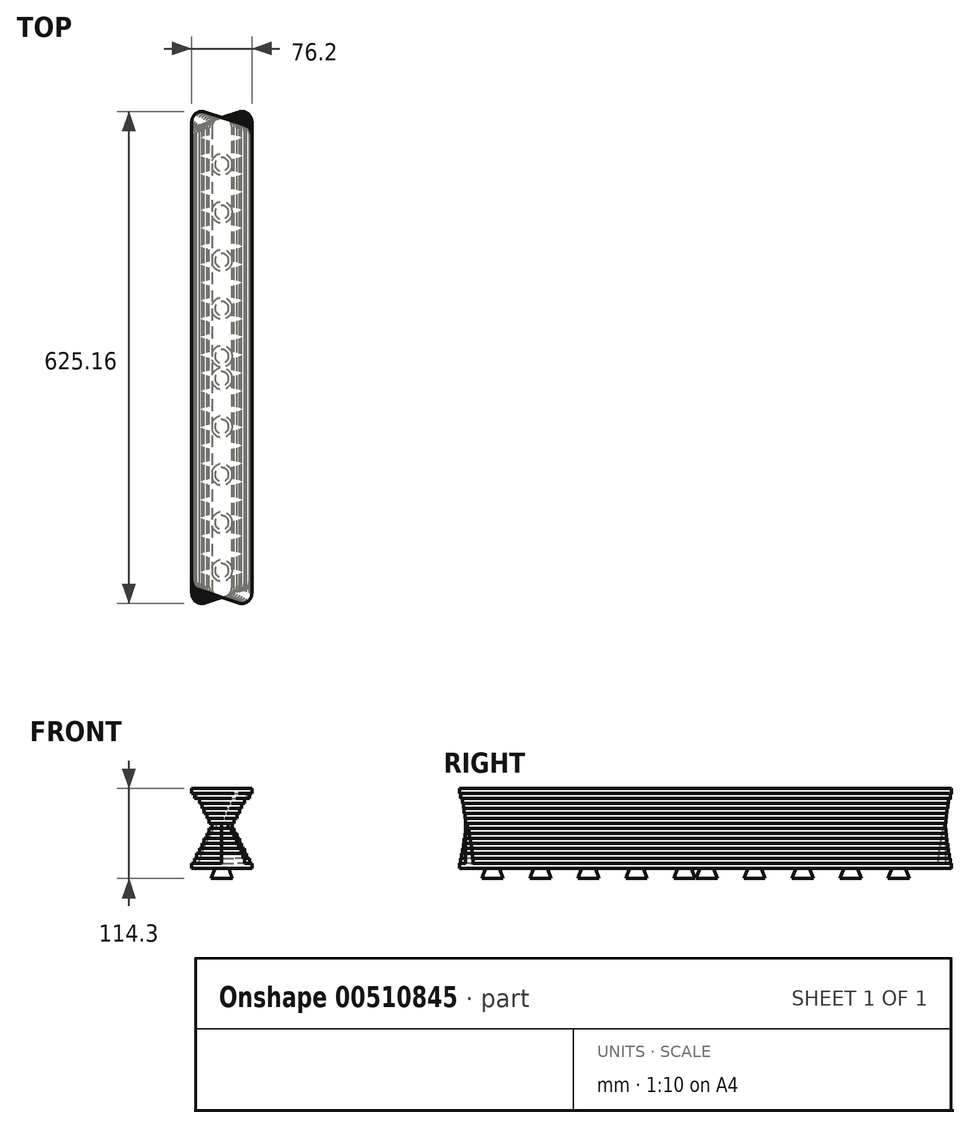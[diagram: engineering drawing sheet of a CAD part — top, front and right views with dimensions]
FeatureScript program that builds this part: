
annotation { "Feature Type Name" : "Feature", "Feature Type Description" : "" }
export const myFeature = defineFeature(function(context is Context, id is Id, definition is map)
    precondition{}
    {
        {
            var Q0;
            Q0=qCreatedBy(makeId("Top.planeOp"),FACE);
            var sketch = newSketch(context, id + "F0", { "sketchPlane" : qUnion([Q0])});
            skPoint(sketch, "E0", {"position": v(0, 0) * mm});
            skPoint(sketch, "E1", {"position": v(-38.1, 0) * mm});
            skPoint(sketch, "E2", {"position": v(-38.1, -304.8) * mm});
            skPoint(sketch, "E3", {"position": v(38.1, 0) * mm});
            skPoint(sketch, "E4", {"position": v(38.1, -279.4) * mm});
            skLineSegment(sketch, "E5", {"start": v(-38.1, 0) * mm, "end": v(-38.1, -287.18) * mm});
            skLineSegment(sketch, "E6", {"start": v(-21.38, -299.23) * mm, "end": v(29.42, -282.3) * mm});
            skLineSegment(sketch, "E7", {"start": v(38.1, -270.25) * mm, "end": v(38.1, 0) * mm});
            skArc(sketch, "E8.filletArc", {"start": v(-38.1, -287.18) * mm, "mid": v(-32.83, -297.48) * mm, "end": v(-21.38, -299.23) * mm});
            skArc(sketch, "E9.filletArc", {"start": v(29.42, -282.3) * mm, "mid": v(35.7, -277.67) * mm, "end": v(38.1, -270.25) * mm});
            skPoint(sketch, "E10", {"position": v(-38.1, 304.8) * mm});
            skPoint(sketch, "E11", {"position": v(38.1, 330.2) * mm});
            skLineSegment(sketch, "E12", {"start": v(-38.1, 0) * mm, "end": v(-38.1, 295.65) * mm});
            skLineSegment(sketch, "E13", {"start": v(-29.42, 307.7) * mm, "end": v(21.38, 324.63) * mm});
            skLineSegment(sketch, "E14", {"start": v(38.1, 312.58) * mm, "end": v(38.1, 0) * mm});
            skArc(sketch, "E15.filletArc", {"start": v(-29.42, 307.7) * mm, "mid": v(-35.7, 303.07) * mm, "end": v(-38.1, 295.65) * mm});
            skArc(sketch, "E16.filletArc", {"start": v(38.1, 312.58) * mm, "mid": v(32.83, 322.88) * mm, "end": v(21.38, 324.63) * mm});
            skSolve(sketch);
        }
        {
            var Q0;
            Q0=makeQuery(id+"F0.imprint","IMPRINT",FACE,{"disambiguationData":[TD([[makeQuery(id+"F0.imprint","IMPRINT",EDGE,{"derivedFrom":sQuery(id+"F0.wireOp",EDGE,"E5")}),1.0]])]});
            extrude(context, id + "F1", {"entities" : qUnion([Q0]), "depth" : 6.35 * mm});
        }
        {
            var Q0;
            Q0=makeQuery(id+"F1.opExtrude","CAP_FACE",FACE,{"disambiguationData":[OSD([sQuery(id+"F0.wireOp",EDGE,"E5"),sQuery(id+"F0.wireOp",EDGE,"E6"),sQuery(id+"F0.wireOp",EDGE,"E7"),sQuery(id+"F0.wireOp",EDGE,"E8.filletArc"),sQuery(id+"F0.wireOp",EDGE,"E9.filletArc"),sQuery(id+"F0.wireOp",EDGE,"E12"),sQuery(id+"F0.wireOp",EDGE,"E13"),sQuery(id+"F0.wireOp",EDGE,"E14"),sQuery(id+"F0.wireOp",EDGE,"E15.filletArc"),sQuery(id+"F0.wireOp",EDGE,"E16.filletArc")])],"isStart":false});
            var sketch = newSketch(context, id + "F2", { "sketchPlane" : qUnion([Q0])});
            skPoint(sketch, "E17", {"position": v(0, 0) * mm});
            skPoint(sketch, "E18", {"position": v(-34.93, 0) * mm});
            skPoint(sketch, "E19", {"position": v(-34.92, -303.21) * mm});
            skPoint(sketch, "E20", {"position": v(34.93, 0) * mm});
            skPoint(sketch, "E21", {"position": v(34.93, -280.99) * mm});
            skLineSegment(sketch, "E22", {"start": v(-34.93, 0) * mm, "end": v(-34.92, -285.84) * mm});
            skLineSegment(sketch, "E23", {"start": v(-18.37, -297.95) * mm, "end": v(26.08, -283.8) * mm});
            skLineSegment(sketch, "E24", {"start": v(34.93, -271.7) * mm, "end": v(34.93, 0) * mm});
            skArc(sketch, "E25.filletArc", {"start": v(-34.92, -285.84) * mm, "mid": v(-29.72, -296.1) * mm, "end": v(-18.37, -297.95) * mm});
            skArc(sketch, "E26.filletArc", {"start": v(26.08, -283.8) * mm, "mid": v(32.48, -279.2) * mm, "end": v(34.92, -271.7) * mm});
            skPoint(sketch, "E27", {"position": v(-34.93, 306.39) * mm});
            skPoint(sketch, "E28", {"position": v(34.92, 328.61) * mm});
            skLineSegment(sketch, "E29", {"start": v(-34.93, 0) * mm, "end": v(-34.93, 297.1) * mm});
            skLineSegment(sketch, "E30", {"start": v(-26.08, 309.2) * mm, "end": v(18.37, 323.35) * mm});
            skLineSegment(sketch, "E31", {"start": v(34.92, 311.24) * mm, "end": v(34.93, 0) * mm});
            skArc(sketch, "E32.filletArc", {"start": v(-26.08, 309.2) * mm, "mid": v(-32.48, 304.6) * mm, "end": v(-34.93, 297.1) * mm});
            skArc(sketch, "E33.filletArc", {"start": v(34.92, 311.24) * mm, "mid": v(29.72, 321.5) * mm, "end": v(18.37, 323.35) * mm});
            skSolve(sketch);
        }
        {
            var Q0;
            {var subQ8=sQuery(id+"F2.wireOp",EDGE,"E22");Q0=makeQuery(id+"F2.imprint","IMPRINT",FACE,{"disambiguationData":[TD([[makeQuery(id+"F2.imprint","IMPRINT",EDGE,{"derivedFrom":subQ8}),1.0]])]});}
            extrude(context, id + "F3", {"entities" : qUnion([Q0]), "depth" : 6.35 * mm});
        }
        {
            var Q0;
            Q0=makeQuery(id+"F3.opExtrude","CAP_FACE",FACE,{"disambiguationData":[OSD([sQuery(id+"F0.wireOp",EDGE,"E6"),sQuery(id+"F0.wireOp",EDGE,"E13"),sQuery(id+"F2.wireOp",EDGE,"E22"),sQuery(id+"F2.wireOp",EDGE,"E23"),sQuery(id+"F2.wireOp",EDGE,"E24"),sQuery(id+"F2.wireOp",EDGE,"E25.filletArc"),sQuery(id+"F2.wireOp",EDGE,"E26.filletArc"),sQuery(id+"F2.wireOp",EDGE,"E29"),sQuery(id+"F2.wireOp",EDGE,"E30"),sQuery(id+"F2.wireOp",EDGE,"E31"),sQuery(id+"F2.wireOp",EDGE,"E32.filletArc"),sQuery(id+"F2.wireOp",EDGE,"E33.filletArc")])],"isStart":false});
            var sketch = newSketch(context, id + "F4", { "sketchPlane" : qUnion([Q0])});
            skPoint(sketch, "E34", {"position": v(0, 0) * mm});
            skPoint(sketch, "E35", {"position": v(-31.75, 0) * mm});
            skPoint(sketch, "E36", {"position": v(-31.75, -301.63) * mm});
            skPoint(sketch, "E37", {"position": v(31.75, 0) * mm});
            skPoint(sketch, "E38", {"position": v(31.75, -282.58) * mm});
            skLineSegment(sketch, "E39", {"start": v(-31.75, 0) * mm, "end": v(-31.75, -284.56) * mm});
            skLineSegment(sketch, "E40", {"start": v(-15.4, -296.72) * mm, "end": v(22.7, -285.3) * mm});
            skLineSegment(sketch, "E41", {"start": v(31.75, -273.13) * mm, "end": v(31.75, 0) * mm});
            skArc(sketch, "E42.filletArc", {"start": v(-31.75, -284.56) * mm, "mid": v(-26.63, -294.74) * mm, "end": v(-15.4, -296.72) * mm});
            skArc(sketch, "E43.filletArc", {"start": v(22.7, -285.3) * mm, "mid": v(29.24, -280.7) * mm, "end": v(31.75, -273.13) * mm});
            skPoint(sketch, "E44.MirrorP", {"position": v(-461.86, 195.96) * mm});
            skPoint(sketch, "E45", {"position": v(-31.75, 307.98) * mm});
            skPoint(sketch, "E46", {"position": v(31.75, 327.03) * mm});
            skLineSegment(sketch, "E47", {"start": v(-31.75, 0) * mm, "end": v(-31.75, 298.53) * mm});
            skLineSegment(sketch, "E48", {"start": v(-22.7, 310.7) * mm, "end": v(15.4, 322.12) * mm});
            skLineSegment(sketch, "E49", {"start": v(31.75, 309.96) * mm, "end": v(31.75, 0) * mm});
            skArc(sketch, "E50.filletArc", {"start": v(-22.7, 310.7) * mm, "mid": v(-29.24, 306.1) * mm, "end": v(-31.75, 298.53) * mm});
            skArc(sketch, "E51.filletArc", {"start": v(31.75, 309.96) * mm, "mid": v(26.63, 320.14) * mm, "end": v(15.4, 322.12) * mm});
            skSolve(sketch);
        }
        {
            var Q0;
            {var subQ8=sQuery(id+"F4.wireOp",EDGE,"E39");Q0=makeQuery(id+"F4.imprint","IMPRINT",FACE,{"disambiguationData":[TD([[makeQuery(id+"F4.imprint","IMPRINT",EDGE,{"derivedFrom":subQ8}),1.0]])]});}
            extrude(context, id + "F5", {"entities" : qUnion([Q0]), "depth" : 6.35 * mm});
        }
        {
            var Q0;
            Q0=makeQuery(id+"F5.opExtrude","CAP_FACE",FACE,{"disambiguationData":[OSD([sQuery(id+"F0.wireOp",EDGE,"E6"),sQuery(id+"F0.wireOp",EDGE,"E13"),sQuery(id+"F4.wireOp",EDGE,"E39"),sQuery(id+"F4.wireOp",EDGE,"E40"),sQuery(id+"F4.wireOp",EDGE,"E41"),sQuery(id+"F4.wireOp",EDGE,"E42.filletArc"),sQuery(id+"F4.wireOp",EDGE,"E43.filletArc"),sQuery(id+"F4.wireOp",EDGE,"E47"),sQuery(id+"F4.wireOp",EDGE,"E48"),sQuery(id+"F4.wireOp",EDGE,"E49"),sQuery(id+"F4.wireOp",EDGE,"E50.filletArc"),sQuery(id+"F4.wireOp",EDGE,"E51.filletArc")])],"isStart":false});
            var sketch = newSketch(context, id + "F6", { "sketchPlane" : qUnion([Q0])});
            skPoint(sketch, "E52", {"position": v(0, 0) * mm});
            skPoint(sketch, "E53", {"position": v(-28.58, 0) * mm});
            skPoint(sketch, "E54", {"position": v(-28.57, -300.04) * mm});
            skPoint(sketch, "E55", {"position": v(28.58, 0) * mm});
            skPoint(sketch, "E56", {"position": v(28.58, -284.16) * mm});
            skLineSegment(sketch, "E57", {"start": v(-28.58, 0) * mm, "end": v(-28.57, -283.33) * mm});
            skLineSegment(sketch, "E58", {"start": v(-12.48, -295.57) * mm, "end": v(19.27, -286.75) * mm});
            skLineSegment(sketch, "E59", {"start": v(28.58, -274.5) * mm, "end": v(28.58, 0) * mm});
            skArc(sketch, "E60.filletArc", {"start": v(-28.57, -283.33) * mm, "mid": v(-23.56, -293.44) * mm, "end": v(-12.48, -295.57) * mm});
            skArc(sketch, "E61.filletArc", {"start": v(19.27, -286.75) * mm, "mid": v(25.99, -282.2) * mm, "end": v(28.57, -274.5) * mm});
            skPoint(sketch, "E62.MirrorP", {"position": v(-895.77, 331.85) * mm});
            skPoint(sketch, "E63", {"position": v(-28.58, 309.56) * mm});
            skPoint(sketch, "E64", {"position": v(28.57, 325.44) * mm});
            skLineSegment(sketch, "E65", {"start": v(-28.58, 0) * mm, "end": v(-28.58, 299.9) * mm});
            skLineSegment(sketch, "E66", {"start": v(-19.27, 312.15) * mm, "end": v(12.48, 320.97) * mm});
            skLineSegment(sketch, "E67", {"start": v(28.57, 308.73) * mm, "end": v(28.58, 0) * mm});
            skArc(sketch, "E68.filletArc", {"start": v(-19.27, 312.15) * mm, "mid": v(-25.99, 307.6) * mm, "end": v(-28.58, 299.9) * mm});
            skArc(sketch, "E69.filletArc", {"start": v(28.57, 308.73) * mm, "mid": v(23.56, 318.84) * mm, "end": v(12.48, 320.97) * mm});
            skSolve(sketch);
        }
        {
            var Q0;
            Q0=makeQuery(id+"F6.imprint","IMPRINT",FACE,{"disambiguationData":[TD([[makeQuery(id+"F6.imprint","IMPRINT",EDGE,{"derivedFrom":sQuery(id+"F6.wireOp",EDGE,"E57")}),1.0]])]});
            extrude(context, id + "F7", {"entities" : qUnion([Q0]), "depth" : 6.35 * mm});
        }
        {
            var Q0;
            Q0=makeQuery(id+"F7.opExtrude","CAP_FACE",FACE,{"disambiguationData":[OSD([sQuery(id+"F0.wireOp",EDGE,"E6"),sQuery(id+"F0.wireOp",EDGE,"E13"),sQuery(id+"F6.wireOp",EDGE,"E57"),sQuery(id+"F6.wireOp",EDGE,"E58"),sQuery(id+"F6.wireOp",EDGE,"E59"),sQuery(id+"F6.wireOp",EDGE,"E60.filletArc"),sQuery(id+"F6.wireOp",EDGE,"E61.filletArc"),sQuery(id+"F6.wireOp",EDGE,"E65"),sQuery(id+"F6.wireOp",EDGE,"E66"),sQuery(id+"F6.wireOp",EDGE,"E67"),sQuery(id+"F6.wireOp",EDGE,"E68.filletArc"),sQuery(id+"F6.wireOp",EDGE,"E69.filletArc")])],"isStart":false});
            var sketch = newSketch(context, id + "F8", { "sketchPlane" : qUnion([Q0])});
            skPoint(sketch, "E70", {"position": v(0, 0) * mm});
            skPoint(sketch, "E71", {"position": v(-25.4, 0) * mm});
            skPoint(sketch, "E72", {"position": v(-25.4, -298.45) * mm});
            skPoint(sketch, "E73", {"position": v(25.4, 0) * mm});
            skPoint(sketch, "E74", {"position": v(25.4, -285.75) * mm});
            skLineSegment(sketch, "E75", {"start": v(-25.4, 0) * mm, "end": v(-25.4, -282.18) * mm});
            skLineSegment(sketch, "E76", {"start": v(-9.62, -294.5) * mm, "end": v(15.78, -288.15) * mm});
            skLineSegment(sketch, "E77", {"start": v(25.4, -275.83) * mm, "end": v(25.4, 0) * mm});
            skArc(sketch, "E78.filletArc", {"start": v(-25.4, -282.18) * mm, "mid": v(-20.52, -292.2) * mm, "end": v(-9.62, -294.5) * mm});
            skArc(sketch, "E79.filletArc", {"start": v(15.78, -288.15) * mm, "mid": v(22.71, -283.65) * mm, "end": v(25.4, -275.83) * mm});
            skPoint(sketch, "E80.MirrorP", {"position": v(-1189.04, 488.26) * mm});
            skPoint(sketch, "E81", {"position": v(-25.4, 311.15) * mm});
            skPoint(sketch, "E82", {"position": v(25.4, 323.85) * mm});
            skLineSegment(sketch, "E83", {"start": v(-25.4, 0) * mm, "end": v(-25.4, 301.23) * mm});
            skLineSegment(sketch, "E84", {"start": v(-15.78, 313.55) * mm, "end": v(9.62, 319.9) * mm});
            skLineSegment(sketch, "E85", {"start": v(25.4, 307.58) * mm, "end": v(25.4, 0) * mm});
            skArc(sketch, "E86.filletArc", {"start": v(-15.78, 313.55) * mm, "mid": v(-22.71, 309.05) * mm, "end": v(-25.4, 301.23) * mm});
            skArc(sketch, "E87.filletArc", {"start": v(25.4, 307.58) * mm, "mid": v(20.52, 317.6) * mm, "end": v(9.62, 319.9) * mm});
            skSolve(sketch);
        }
        {
            var Q0;
            Q0=makeQuery(id+"F8.imprint","IMPRINT",FACE,{"disambiguationData":[TD([[makeQuery(id+"F8.imprint","IMPRINT",EDGE,{"derivedFrom":sQuery(id+"F8.wireOp",EDGE,"E75")}),1.0]])]});
            extrude(context, id + "F9", {"entities" : qUnion([Q0]), "depth" : 6.35 * mm});
        }
        {
            var Q0;
            Q0=makeQuery(id+"F9.opExtrude","CAP_FACE",FACE,{"disambiguationData":[OSD([sQuery(id+"F0.wireOp",EDGE,"E6"),sQuery(id+"F0.wireOp",EDGE,"E13"),sQuery(id+"F8.wireOp",EDGE,"E75"),sQuery(id+"F8.wireOp",EDGE,"E76"),sQuery(id+"F8.wireOp",EDGE,"E77"),sQuery(id+"F8.wireOp",EDGE,"E78.filletArc"),sQuery(id+"F8.wireOp",EDGE,"E79.filletArc"),sQuery(id+"F8.wireOp",EDGE,"E83"),sQuery(id+"F8.wireOp",EDGE,"E84"),sQuery(id+"F8.wireOp",EDGE,"E85"),sQuery(id+"F8.wireOp",EDGE,"E86.filletArc"),sQuery(id+"F8.wireOp",EDGE,"E87.filletArc")])],"isStart":false});
            var sketch = newSketch(context, id + "F10", { "sketchPlane" : qUnion([Q0])});
            skPoint(sketch, "E88", {"position": v(0, 0) * mm});
            skPoint(sketch, "E89", {"position": v(-22.23, 0) * mm});
            skPoint(sketch, "E90", {"position": v(-22.22, -296.86) * mm});
            skPoint(sketch, "E91", {"position": v(22.23, 0) * mm});
            skPoint(sketch, "E92", {"position": v(22.23, -287.34) * mm});
            skLineSegment(sketch, "E93", {"start": v(-22.23, 0) * mm, "end": v(-22.22, -281.15) * mm});
            skLineSegment(sketch, "E94", {"start": v(-6.86, -293.57) * mm, "end": v(12.19, -289.49) * mm});
            skLineSegment(sketch, "E95", {"start": v(22.23, -277.07) * mm, "end": v(22.23, 0) * mm});
            skArc(sketch, "E96.filletArc", {"start": v(-22.22, -281.15) * mm, "mid": v(-17.5, -291.03) * mm, "end": v(-6.86, -293.57) * mm});
            skArc(sketch, "E97.filletArc", {"start": v(12.19, -289.49) * mm, "mid": v(19.4, -285.05) * mm, "end": v(22.22, -277.07) * mm});
            skPoint(sketch, "E98.MirrorP", {"position": v(-1110.6, 407.11) * mm});
            skPoint(sketch, "E99", {"position": v(-22.23, 312.74) * mm});
            skPoint(sketch, "E100", {"position": v(22.22, 322.26) * mm});
            skLineSegment(sketch, "E101", {"start": v(-22.23, 0) * mm, "end": v(-22.23, 302.47) * mm});
            skLineSegment(sketch, "E102", {"start": v(-12.19, 314.89) * mm, "end": v(6.86, 318.97) * mm});
            skLineSegment(sketch, "E103", {"start": v(22.22, 306.55) * mm, "end": v(22.23, 0) * mm});
            skArc(sketch, "E104.filletArc", {"start": v(-12.19, 314.89) * mm, "mid": v(-19.4, 310.45) * mm, "end": v(-22.23, 302.47) * mm});
            skArc(sketch, "E105.filletArc", {"start": v(22.22, 306.55) * mm, "mid": v(17.5, 316.43) * mm, "end": v(6.86, 318.97) * mm});
            skSolve(sketch);
        }
        {
            var Q0;
            Q0=makeQuery(id+"F10.imprint","IMPRINT",FACE,{"disambiguationData":[TD([[makeQuery(id+"F10.imprint","IMPRINT",EDGE,{"derivedFrom":sQuery(id+"F10.wireOp",EDGE,"E93")}),1.0]])]});
            extrude(context, id + "F11", {"entities" : qUnion([Q0]), "depth" : 6.35 * mm});
        }
        {
            var Q0;
            Q0=makeQuery(id+"F11.opExtrude","CAP_FACE",FACE,{"disambiguationData":[OSD([sQuery(id+"F0.wireOp",EDGE,"E6"),sQuery(id+"F0.wireOp",EDGE,"E13"),sQuery(id+"F10.wireOp",EDGE,"E93"),sQuery(id+"F10.wireOp",EDGE,"E94"),sQuery(id+"F10.wireOp",EDGE,"E95"),sQuery(id+"F10.wireOp",EDGE,"E96.filletArc"),sQuery(id+"F10.wireOp",EDGE,"E97.filletArc"),sQuery(id+"F10.wireOp",EDGE,"E101"),sQuery(id+"F10.wireOp",EDGE,"E102"),sQuery(id+"F10.wireOp",EDGE,"E103"),sQuery(id+"F10.wireOp",EDGE,"E104.filletArc"),sQuery(id+"F10.wireOp",EDGE,"E105.filletArc")])],"isStart":false});
            var sketch = newSketch(context, id + "F12", { "sketchPlane" : qUnion([Q0])});
            skPoint(sketch, "E106", {"position": v(0, 0) * mm});
            skPoint(sketch, "E107", {"position": v(-19.05, 0) * mm});
            skPoint(sketch, "E108", {"position": v(-19.05, -295.28) * mm});
            skPoint(sketch, "E109", {"position": v(19.05, 0) * mm});
            skPoint(sketch, "E110", {"position": v(19.05, -288.93) * mm});
            skLineSegment(sketch, "E111", {"start": v(-19.05, 0) * mm, "end": v(-19.05, -280.28) * mm});
            skLineSegment(sketch, "E112", {"start": v(-4.26, -292.81) * mm, "end": v(8.44, -290.7) * mm});
            skLineSegment(sketch, "E113", {"start": v(19.05, -278.17) * mm, "end": v(19.05, 0) * mm});
            skArc(sketch, "E114.filletArc", {"start": v(-19.05, -280.28) * mm, "mid": v(-14.56, -289.97) * mm, "end": v(-4.26, -292.81) * mm});
            skArc(sketch, "E115.filletArc", {"start": v(8.44, -290.7) * mm, "mid": v(16.04, -286.38) * mm, "end": v(19.05, -278.17) * mm});
            skPoint(sketch, "E116.MirrorP", {"position": v(-1134.4, 517.38) * mm});
            skPoint(sketch, "E117", {"position": v(-19.05, 314.33) * mm});
            skPoint(sketch, "E118", {"position": v(19.05, 320.68) * mm});
            skLineSegment(sketch, "E119", {"start": v(-19.05, 0) * mm, "end": v(-19.05, 303.57) * mm});
            skLineSegment(sketch, "E120", {"start": v(-8.44, 316.1) * mm, "end": v(4.26, 318.21) * mm});
            skLineSegment(sketch, "E121", {"start": v(19.05, 305.68) * mm, "end": v(19.05, 0) * mm});
            skArc(sketch, "E122.filletArc", {"start": v(-8.44, 316.1) * mm, "mid": v(-16.04, 311.78) * mm, "end": v(-19.05, 303.57) * mm});
            skArc(sketch, "E123.filletArc", {"start": v(19.05, 305.68) * mm, "mid": v(14.56, 315.37) * mm, "end": v(4.26, 318.21) * mm});
            skSolve(sketch);
        }
        {
            var Q0;
            {var subQ12=sQuery(id+"F12.wireOp",EDGE,"E113");Q0=makeQuery(id+"F12.imprint","IMPRINT",FACE,{"disambiguationData":[TD([[makeQuery(id+"F12.imprint","IMPRINT",EDGE,{"derivedFrom":subQ12}),1.0]])]});}
            extrude(context, id + "F13", {"entities" : qUnion([Q0]), "depth" : 6.35 * mm});
        }
        {
            var Q0;
            Q0=makeQuery(id+"F13.opExtrude","CAP_FACE",FACE,{"disambiguationData":[OSD([sQuery(id+"F0.wireOp",EDGE,"E6"),sQuery(id+"F0.wireOp",EDGE,"E13"),sQuery(id+"F10.wireOp",EDGE,"E93"),sQuery(id+"F10.wireOp",EDGE,"E96.filletArc"),sQuery(id+"F10.wireOp",EDGE,"E101"),sQuery(id+"F10.wireOp",EDGE,"E102"),sQuery(id+"F10.wireOp",EDGE,"E104.filletArc"),sQuery(id+"F12.wireOp",EDGE,"E112"),sQuery(id+"F12.wireOp",EDGE,"E113"),sQuery(id+"F12.wireOp",EDGE,"E115.filletArc"),sQuery(id+"F12.wireOp",EDGE,"E121"),sQuery(id+"F12.wireOp",EDGE,"E123.filletArc")])],"isStart":false});
            var sketch = newSketch(context, id + "F14", { "sketchPlane" : qUnion([Q0])});
            skPoint(sketch, "E124", {"position": v(0, 0) * mm});
            skPoint(sketch, "E125", {"position": v(-15.88, 0) * mm});
            skPoint(sketch, "E126", {"position": v(-15.87, -293.69) * mm});
            skPoint(sketch, "E127", {"position": v(15.88, 0) * mm});
            skPoint(sketch, "E128", {"position": v(15.88, -290.51) * mm});
            skLineSegment(sketch, "E129", {"start": v(-15.88, 0) * mm, "end": v(-15.87, -279.65) * mm});
            skLineSegment(sketch, "E130", {"start": v(-1.91, -292.3) * mm, "end": v(4.44, -291.66) * mm});
            skLineSegment(sketch, "E131", {"start": v(15.88, -279.02) * mm, "end": v(15.88, 0) * mm});
            skArc(sketch, "E132.filletArc", {"start": v(-15.87, -279.65) * mm, "mid": v(-11.7, -289.07) * mm, "end": v(-1.91, -292.3) * mm});
            skArc(sketch, "E133.filletArc", {"start": v(4.44, -291.66) * mm, "mid": v(12.6, -287.54) * mm, "end": v(15.88, -279.02) * mm});
            skPoint(sketch, "E134.MirrorP", {"position": v(-1354.1, 474.43) * mm});
            skPoint(sketch, "E135", {"position": v(-15.88, 315.91) * mm});
            skPoint(sketch, "E136", {"position": v(15.87, 319.09) * mm});
            skLineSegment(sketch, "E137", {"start": v(-15.88, 0) * mm, "end": v(-15.88, 304.42) * mm});
            skLineSegment(sketch, "E138", {"start": v(-4.44, 317.06) * mm, "end": v(1.91, 317.7) * mm});
            skLineSegment(sketch, "E139", {"start": v(15.87, 305.05) * mm, "end": v(15.88, 0) * mm});
            skArc(sketch, "E140.filletArc", {"start": v(-4.44, 317.06) * mm, "mid": v(-12.6, 312.94) * mm, "end": v(-15.88, 304.42) * mm});
            skArc(sketch, "E141.filletArc", {"start": v(15.87, 305.05) * mm, "mid": v(11.7, 314.47) * mm, "end": v(1.91, 317.7) * mm});
            skSolve(sketch);
        }
        {
            var Q0;
            Q0=makeQuery(id+"F14.imprint","IMPRINT",FACE,{"disambiguationData":[TD([[makeQuery(id+"F14.imprint","IMPRINT",EDGE,{"derivedFrom":sQuery(id+"F14.wireOp",EDGE,"E129")}),1.0]])]});
            extrude(context, id + "F15", {"entities" : qUnion([Q0]), "depth" : 6.35 * mm});
        }
        {
            var Q0;
            Q0=makeQuery(id+"F15.opExtrude","CAP_FACE",FACE,{"disambiguationData":[OSD([sQuery(id+"F0.wireOp",EDGE,"E6"),sQuery(id+"F0.wireOp",EDGE,"E13"),sQuery(id+"F14.wireOp",EDGE,"E129"),sQuery(id+"F14.wireOp",EDGE,"E130"),sQuery(id+"F14.wireOp",EDGE,"E131"),sQuery(id+"F14.wireOp",EDGE,"E132.filletArc"),sQuery(id+"F14.wireOp",EDGE,"E133.filletArc"),sQuery(id+"F14.wireOp",EDGE,"E137"),sQuery(id+"F14.wireOp",EDGE,"E138"),sQuery(id+"F14.wireOp",EDGE,"E139"),sQuery(id+"F14.wireOp",EDGE,"E140.filletArc"),sQuery(id+"F14.wireOp",EDGE,"E141.filletArc")])],"isStart":false});
            var sketch = newSketch(context, id + "F16", { "sketchPlane" : qUnion([Q0])});
            skPoint(sketch, "E142", {"position": v(0, 0) * mm});
            skPoint(sketch, "E143", {"position": v(-12.7, 0) * mm});
            skPoint(sketch, "E144", {"position": v(-12.7, -292.1) * mm});
            skPoint(sketch, "E145", {"position": v(12.7, 0) * mm});
            skPoint(sketch, "E146", {"position": v(12.7, -292.1) * mm});
            skLineSegment(sketch, "E147", {"start": v(-12.7, 0) * mm, "end": v(-12.7, -279.4) * mm});
            skLineSegment(sketch, "E148", {"start": v(0, -292.1) * mm, "end": v(0, -292.1) * mm});
            skLineSegment(sketch, "E149", {"start": v(12.7, -279.4) * mm, "end": v(12.7, 0) * mm});
            skArc(sketch, "E150.filletArc", {"start": v(-12.7, -279.4) * mm, "mid": v(-8.98, -288.38) * mm, "end": v(0, -292.1) * mm});
            skArc(sketch, "E151.filletArc", {"start": v(0, -292.1) * mm, "mid": v(8.98, -288.38) * mm, "end": v(12.7, -279.4) * mm});
            skPoint(sketch, "E152.MirrorP", {"position": v(-1174.77, 259.43) * mm});
            skPoint(sketch, "E153", {"position": v(-12.7, 317.5) * mm});
            skPoint(sketch, "E154", {"position": v(12.7, 317.5) * mm});
            skLineSegment(sketch, "E155", {"start": v(-12.7, 0) * mm, "end": v(-12.7, 304.8) * mm});
            skLineSegment(sketch, "E156", {"start": v(0, 317.5) * mm, "end": v(0, 317.5) * mm});
            skLineSegment(sketch, "E157", {"start": v(12.7, 304.8) * mm, "end": v(12.7, 0) * mm});
            skArc(sketch, "E158.filletArc", {"start": v(0, 317.5) * mm, "mid": v(-8.98, 313.78) * mm, "end": v(-12.7, 304.8) * mm});
            skArc(sketch, "E159.filletArc", {"start": v(12.7, 304.8) * mm, "mid": v(8.98, 313.78) * mm, "end": v(0, 317.5) * mm});
            skSolve(sketch);
        }
        {
            var Q0;
            Q0=makeQuery(id+"F16.imprint","IMPRINT",FACE,{"disambiguationData":[TD([[makeQuery(id+"F16.imprint","IMPRINT",EDGE,{"derivedFrom":sQuery(id+"F16.wireOp",EDGE,"E147")}),1.0]])]});
            extrude(context, id + "F17", {"entities" : qUnion([Q0]), "depth" : 6.35 * mm});
        }
        {
            var Q0;
            Q0=makeQuery(id+"F17.opExtrude","CAP_FACE",FACE,{"disambiguationData":[OSD([sQuery(id+"F0.wireOp",EDGE,"E6"),sQuery(id+"F0.wireOp",EDGE,"E13"),sQuery(id+"F16.wireOp",EDGE,"E147"),sQuery(id+"F16.wireOp",EDGE,"E149"),sQuery(id+"F16.wireOp",EDGE,"E150.filletArc"),sQuery(id+"F16.wireOp",EDGE,"E151.filletArc"),sQuery(id+"F16.wireOp",EDGE,"E155"),sQuery(id+"F16.wireOp",EDGE,"E157"),sQuery(id+"F16.wireOp",EDGE,"E158.filletArc"),sQuery(id+"F16.wireOp",EDGE,"E159.filletArc")])],"isStart":false});
            var sketch = newSketch(context, id + "F18", { "sketchPlane" : qUnion([Q0])});
            skPoint(sketch, "E160", {"position": v(0, 0) * mm});
            skPoint(sketch, "E161", {"position": v(-15.88, 0) * mm});
            skPoint(sketch, "E162", {"position": v(-15.87, -290.51) * mm});
            skPoint(sketch, "E163", {"position": v(15.88, 0) * mm});
            skPoint(sketch, "E164", {"position": v(15.88, -293.69) * mm});
            skLineSegment(sketch, "E165", {"start": v(-15.88, 0) * mm, "end": v(-15.87, -279.02) * mm});
            skLineSegment(sketch, "E166", {"start": v(-4.44, -291.66) * mm, "end": v(1.91, -292.3) * mm});
            skLineSegment(sketch, "E167", {"start": v(15.88, -279.65) * mm, "end": v(15.88, 0) * mm});
            skArc(sketch, "E168.filletArc", {"start": v(-15.87, -279.02) * mm, "mid": v(-12.6, -287.54) * mm, "end": v(-4.44, -291.66) * mm});
            skArc(sketch, "E169.filletArc", {"start": v(1.91, -292.3) * mm, "mid": v(11.7, -289.07) * mm, "end": v(15.87, -279.65) * mm});
            skPoint(sketch, "E170.MirrorP", {"position": v(-1386.88, 490.35) * mm});
            skPoint(sketch, "E171", {"position": v(-15.88, 319.09) * mm});
            skPoint(sketch, "E172", {"position": v(15.87, 315.91) * mm});
            skLineSegment(sketch, "E173", {"start": v(-15.88, 0) * mm, "end": v(-15.88, 305.05) * mm});
            skLineSegment(sketch, "E174", {"start": v(-1.91, 317.7) * mm, "end": v(4.44, 317.06) * mm});
            skLineSegment(sketch, "E175", {"start": v(15.87, 304.42) * mm, "end": v(15.88, 0) * mm});
            skArc(sketch, "E176.filletArc", {"start": v(-1.91, 317.7) * mm, "mid": v(-11.7, 314.47) * mm, "end": v(-15.88, 305.05) * mm});
            skArc(sketch, "E177.filletArc", {"start": v(15.87, 304.42) * mm, "mid": v(12.6, 312.94) * mm, "end": v(4.44, 317.06) * mm});
            skSolve(sketch);
        }
        {
            var Q0;
            Q0=qSketchRegion(id+"F18",true);
            extrude(context, id + "F19", {"entities" : qUnion([Q0]), "depth" : 6.35 * mm});
        }
        {
            var Q0;
            Q0=makeQuery(id+"F19.opExtrude","CAP_FACE",FACE,{"disambiguationData":[OSD([sQuery(id+"F0.wireOp",EDGE,"E6"),sQuery(id+"F0.wireOp",EDGE,"E13"),sQuery(id+"F16.wireOp",EDGE,"E147"),sQuery(id+"F16.wireOp",EDGE,"E149"),sQuery(id+"F16.wireOp",EDGE,"E150.filletArc"),sQuery(id+"F16.wireOp",EDGE,"E151.filletArc"),sQuery(id+"F16.wireOp",EDGE,"E155"),sQuery(id+"F16.wireOp",EDGE,"E157"),sQuery(id+"F16.wireOp",EDGE,"E158.filletArc"),sQuery(id+"F16.wireOp",EDGE,"E159.filletArc"),sQuery(id+"F18.wireOp",EDGE,"E166"),sQuery(id+"F18.wireOp",EDGE,"E174")])],"isStart":false});
            var sketch = newSketch(context, id + "F20", { "sketchPlane" : qUnion([Q0])});
            skPoint(sketch, "E178", {"position": v(0, 0) * mm});
            skPoint(sketch, "E179", {"position": v(-19.05, 0) * mm});
            skPoint(sketch, "E180", {"position": v(-19.05, -288.93) * mm});
            skPoint(sketch, "E181", {"position": v(19.05, 0) * mm});
            skPoint(sketch, "E182", {"position": v(19.05, -295.28) * mm});
            skLineSegment(sketch, "E183", {"start": v(-19.05, 0) * mm, "end": v(-19.05, -278.17) * mm});
            skLineSegment(sketch, "E184", {"start": v(-8.44, -290.7) * mm, "end": v(4.26, -292.81) * mm});
            skLineSegment(sketch, "E185", {"start": v(19.05, -280.28) * mm, "end": v(19.05, 0) * mm});
            skArc(sketch, "E186.filletArc", {"start": v(-19.05, -278.17) * mm, "mid": v(-16.04, -286.38) * mm, "end": v(-8.44, -290.7) * mm});
            skArc(sketch, "E187.filletArc", {"start": v(4.26, -292.81) * mm, "mid": v(14.56, -289.97) * mm, "end": v(19.05, -280.28) * mm});
            skPoint(sketch, "E188.MirrorP", {"position": v(-2251.33, 639) * mm});
            skPoint(sketch, "E189", {"position": v(-19.05, 320.68) * mm});
            skPoint(sketch, "E190", {"position": v(19.05, 314.33) * mm});
            skLineSegment(sketch, "E191", {"start": v(-19.05, 0) * mm, "end": v(-19.05, 305.68) * mm});
            skLineSegment(sketch, "E192", {"start": v(-4.26, 318.21) * mm, "end": v(8.44, 316.1) * mm});
            skLineSegment(sketch, "E193", {"start": v(19.05, 303.57) * mm, "end": v(19.05, 0) * mm});
            skArc(sketch, "E194.filletArc", {"start": v(-4.26, 318.21) * mm, "mid": v(-14.56, 315.37) * mm, "end": v(-19.05, 305.68) * mm});
            skArc(sketch, "E195.filletArc", {"start": v(19.05, 303.57) * mm, "mid": v(16.04, 311.78) * mm, "end": v(8.44, 316.1) * mm});
            skSolve(sketch);
        }
        {
            var Q0;
            Q0=qSketchRegion(id+"F20",true);
            extrude(context, id + "F21", {"entities" : qUnion([Q0]), "depth" : 6.35 * mm});
        }
        {
            var Q0;
            Q0=makeQuery(id+"F21.opExtrude","CAP_FACE",FACE,{"disambiguationData":[OSD([sQuery(id+"F0.wireOp",EDGE,"E6"),sQuery(id+"F0.wireOp",EDGE,"E13"),sQuery(id+"F16.wireOp",EDGE,"E147"),sQuery(id+"F16.wireOp",EDGE,"E149"),sQuery(id+"F16.wireOp",EDGE,"E150.filletArc"),sQuery(id+"F16.wireOp",EDGE,"E151.filletArc"),sQuery(id+"F16.wireOp",EDGE,"E155"),sQuery(id+"F16.wireOp",EDGE,"E157"),sQuery(id+"F16.wireOp",EDGE,"E158.filletArc"),sQuery(id+"F16.wireOp",EDGE,"E159.filletArc"),sQuery(id+"F20.wireOp",EDGE,"E184"),sQuery(id+"F20.wireOp",EDGE,"E192")])],"isStart":false});
            var sketch = newSketch(context, id + "F22", { "sketchPlane" : qUnion([Q0])});
            skPoint(sketch, "E196", {"position": v(0, 0) * mm});
            skPoint(sketch, "E197", {"position": v(-22.23, 0) * mm});
            skPoint(sketch, "E198", {"position": v(-22.22, -287.34) * mm});
            skPoint(sketch, "E199", {"position": v(22.23, 0) * mm});
            skPoint(sketch, "E200", {"position": v(22.23, -296.86) * mm});
            skLineSegment(sketch, "E201", {"start": v(-22.23, 0) * mm, "end": v(-22.22, -277.07) * mm});
            skLineSegment(sketch, "E202", {"start": v(-12.19, -289.49) * mm, "end": v(6.86, -293.57) * mm});
            skLineSegment(sketch, "E203", {"start": v(22.23, -281.15) * mm, "end": v(22.23, 0) * mm});
            skArc(sketch, "E204.filletArc", {"start": v(-22.22, -277.07) * mm, "mid": v(-19.4, -285.05) * mm, "end": v(-12.19, -289.49) * mm});
            skArc(sketch, "E205.filletArc", {"start": v(6.86, -293.57) * mm, "mid": v(17.5, -291.03) * mm, "end": v(22.22, -281.15) * mm});
            skPoint(sketch, "E206.MirrorP", {"position": v(-2054.65, 833.78) * mm});
            skPoint(sketch, "E207", {"position": v(-22.23, 322.26) * mm});
            skPoint(sketch, "E208", {"position": v(22.22, 312.74) * mm});
            skLineSegment(sketch, "E209", {"start": v(-22.23, 0) * mm, "end": v(-22.23, 306.55) * mm});
            skLineSegment(sketch, "E210", {"start": v(-6.86, 318.97) * mm, "end": v(12.19, 314.89) * mm});
            skLineSegment(sketch, "E211", {"start": v(22.22, 302.47) * mm, "end": v(22.23, 0) * mm});
            skArc(sketch, "E212.filletArc", {"start": v(-6.86, 318.97) * mm, "mid": v(-17.5, 316.43) * mm, "end": v(-22.23, 306.55) * mm});
            skArc(sketch, "E213.filletArc", {"start": v(22.22, 302.47) * mm, "mid": v(19.4, 310.45) * mm, "end": v(12.19, 314.89) * mm});
            skSolve(sketch);
        }
        {
            var Q0;
            Q0=qSketchRegion(id+"F22",true);
            extrude(context, id + "F23", {"entities" : qUnion([Q0]), "depth" : 6.35 * mm});
        }
        {
            var Q0;
            Q0=makeQuery(id+"F23.opExtrude","CAP_FACE",FACE,{"disambiguationData":[OSD([sQuery(id+"F22.wireOp",EDGE,"E201"),sQuery(id+"F22.wireOp",EDGE,"E202"),sQuery(id+"F22.wireOp",EDGE,"E203"),sQuery(id+"F22.wireOp",EDGE,"E204.filletArc"),sQuery(id+"F22.wireOp",EDGE,"E205.filletArc"),sQuery(id+"F22.wireOp",EDGE,"E209"),sQuery(id+"F22.wireOp",EDGE,"E210"),sQuery(id+"F22.wireOp",EDGE,"E211"),sQuery(id+"F22.wireOp",EDGE,"E212.filletArc"),sQuery(id+"F22.wireOp",EDGE,"E213.filletArc")])],"isStart":false});
            var sketch = newSketch(context, id + "F24", { "sketchPlane" : qUnion([Q0])});
            skPoint(sketch, "E214", {"position": v(0, 0) * mm});
            skPoint(sketch, "E215", {"position": v(-25.4, 0) * mm});
            skPoint(sketch, "E216", {"position": v(-25.4, -285.75) * mm});
            skPoint(sketch, "E217", {"position": v(25.4, 0) * mm});
            skPoint(sketch, "E218", {"position": v(25.4, -298.45) * mm});
            skLineSegment(sketch, "E219", {"start": v(-25.4, 0) * mm, "end": v(-25.4, -275.83) * mm});
            skLineSegment(sketch, "E220", {"start": v(-15.78, -288.15) * mm, "end": v(9.62, -294.5) * mm});
            skLineSegment(sketch, "E221", {"start": v(25.4, -282.18) * mm, "end": v(25.4, 0) * mm});
            skArc(sketch, "E222.filletArc", {"start": v(-25.4, -275.83) * mm, "mid": v(-22.71, -283.65) * mm, "end": v(-15.78, -288.15) * mm});
            skArc(sketch, "E223.filletArc", {"start": v(9.62, -294.5) * mm, "mid": v(20.52, -292.2) * mm, "end": v(25.4, -282.18) * mm});
            skPoint(sketch, "E224.MirrorP", {"position": v(-1763.83, 631.7) * mm});
            skPoint(sketch, "E225", {"position": v(-25.4, 323.85) * mm});
            skPoint(sketch, "E226", {"position": v(25.4, 311.15) * mm});
            skLineSegment(sketch, "E227", {"start": v(-25.4, 0) * mm, "end": v(-25.4, 307.58) * mm});
            skLineSegment(sketch, "E228", {"start": v(-9.62, 319.9) * mm, "end": v(15.78, 313.55) * mm});
            skLineSegment(sketch, "E229", {"start": v(25.4, 301.23) * mm, "end": v(25.4, 0) * mm});
            skArc(sketch, "E230.filletArc", {"start": v(-9.62, 319.9) * mm, "mid": v(-20.52, 317.6) * mm, "end": v(-25.4, 307.58) * mm});
            skArc(sketch, "E231.filletArc", {"start": v(25.4, 301.23) * mm, "mid": v(22.71, 309.05) * mm, "end": v(15.78, 313.55) * mm});
            skSolve(sketch);
        }
        {
            var Q0;
            Q0=qSketchRegion(id+"F24",true);
            extrude(context, id + "F25", {"entities" : qUnion([Q0]), "depth" : 6.35 * mm});
        }
        {
            var Q0;
            Q0=makeQuery(id+"F25.opExtrude","CAP_FACE",FACE,{"disambiguationData":[OSD([sQuery(id+"F24.wireOp",EDGE,"E219"),sQuery(id+"F24.wireOp",EDGE,"E220"),sQuery(id+"F24.wireOp",EDGE,"E221"),sQuery(id+"F24.wireOp",EDGE,"E222.filletArc"),sQuery(id+"F24.wireOp",EDGE,"E223.filletArc"),sQuery(id+"F24.wireOp",EDGE,"E227"),sQuery(id+"F24.wireOp",EDGE,"E228"),sQuery(id+"F24.wireOp",EDGE,"E229"),sQuery(id+"F24.wireOp",EDGE,"E230.filletArc"),sQuery(id+"F24.wireOp",EDGE,"E231.filletArc")])],"isStart":false});
            var sketch = newSketch(context, id + "F26", { "sketchPlane" : qUnion([Q0])});
            skPoint(sketch, "E232", {"position": v(0, 0) * mm});
            skPoint(sketch, "E233", {"position": v(-28.58, 0) * mm});
            skPoint(sketch, "E234", {"position": v(-28.57, -284.16) * mm});
            skPoint(sketch, "E235", {"position": v(28.58, 0) * mm});
            skPoint(sketch, "E236", {"position": v(28.58, -300.04) * mm});
            skLineSegment(sketch, "E237", {"start": v(-28.58, 0) * mm, "end": v(-28.57, -274.5) * mm});
            skLineSegment(sketch, "E238", {"start": v(-19.27, -286.75) * mm, "end": v(12.48, -295.57) * mm});
            skLineSegment(sketch, "E239", {"start": v(28.58, -283.33) * mm, "end": v(28.58, 0) * mm});
            skArc(sketch, "E240.filletArc", {"start": v(-28.57, -274.5) * mm, "mid": v(-25.99, -282.2) * mm, "end": v(-19.27, -286.75) * mm});
            skArc(sketch, "E241.filletArc", {"start": v(12.48, -295.57) * mm, "mid": v(23.56, -293.44) * mm, "end": v(28.57, -283.33) * mm});
            skPoint(sketch, "E242.MirrorP", {"position": v(-2122.86, 677.9) * mm});
            skPoint(sketch, "E243", {"position": v(-28.58, 325.44) * mm});
            skPoint(sketch, "E244", {"position": v(28.57, 309.56) * mm});
            skLineSegment(sketch, "E245", {"start": v(-28.58, 0) * mm, "end": v(-28.58, 308.73) * mm});
            skLineSegment(sketch, "E246", {"start": v(-12.48, 320.97) * mm, "end": v(19.27, 312.15) * mm});
            skLineSegment(sketch, "E247", {"start": v(28.57, 299.9) * mm, "end": v(28.58, 0) * mm});
            skArc(sketch, "E248.filletArc", {"start": v(-12.48, 320.97) * mm, "mid": v(-23.56, 318.84) * mm, "end": v(-28.58, 308.73) * mm});
            skArc(sketch, "E249.filletArc", {"start": v(28.57, 299.9) * mm, "mid": v(25.99, 307.6) * mm, "end": v(19.27, 312.15) * mm});
            skSolve(sketch);
        }
        {
            var Q0;
            Q0=qSketchRegion(id+"F26",true);
            extrude(context, id + "F27", {"entities" : qUnion([Q0]), "depth" : 6.35 * mm});
        }
        {
            var Q0;
            Q0=makeQuery(id+"F27.opExtrude","CAP_FACE",FACE,{"disambiguationData":[OSD([sQuery(id+"F26.wireOp",EDGE,"E237"),sQuery(id+"F26.wireOp",EDGE,"E238"),sQuery(id+"F26.wireOp",EDGE,"E239"),sQuery(id+"F26.wireOp",EDGE,"E240.filletArc"),sQuery(id+"F26.wireOp",EDGE,"E241.filletArc"),sQuery(id+"F26.wireOp",EDGE,"E245"),sQuery(id+"F26.wireOp",EDGE,"E246"),sQuery(id+"F26.wireOp",EDGE,"E247"),sQuery(id+"F26.wireOp",EDGE,"E248.filletArc"),sQuery(id+"F26.wireOp",EDGE,"E249.filletArc")])],"isStart":false});
            var sketch = newSketch(context, id + "F28", { "sketchPlane" : qUnion([Q0])});
            skPoint(sketch, "E250", {"position": v(0, 0) * mm});
            skPoint(sketch, "E251", {"position": v(-31.75, 0) * mm});
            skPoint(sketch, "E252", {"position": v(-31.75, -282.58) * mm});
            skPoint(sketch, "E253", {"position": v(31.75, 0) * mm});
            skPoint(sketch, "E254", {"position": v(31.75, -301.63) * mm});
            skLineSegment(sketch, "E255", {"start": v(-31.75, 0) * mm, "end": v(-31.75, -273.13) * mm});
            skLineSegment(sketch, "E256", {"start": v(-22.7, -285.3) * mm, "end": v(15.4, -296.72) * mm});
            skLineSegment(sketch, "E257", {"start": v(31.75, -284.56) * mm, "end": v(31.75, 0) * mm});
            skArc(sketch, "E258.filletArc", {"start": v(-31.75, -273.13) * mm, "mid": v(-29.24, -280.7) * mm, "end": v(-22.7, -285.3) * mm});
            skArc(sketch, "E259.filletArc", {"start": v(15.4, -296.72) * mm, "mid": v(26.63, -294.74) * mm, "end": v(31.75, -284.56) * mm});
            skPoint(sketch, "E260.MirrorP", {"position": v(-2131.05, 728.59) * mm});
            skPoint(sketch, "E261", {"position": v(-31.75, 327.03) * mm});
            skPoint(sketch, "E262", {"position": v(31.75, 307.98) * mm});
            skLineSegment(sketch, "E263", {"start": v(-31.75, 0) * mm, "end": v(-31.75, 309.96) * mm});
            skLineSegment(sketch, "E264", {"start": v(-15.4, 322.12) * mm, "end": v(22.7, 310.7) * mm});
            skLineSegment(sketch, "E265", {"start": v(31.75, 298.53) * mm, "end": v(31.75, 0) * mm});
            skArc(sketch, "E266.filletArc", {"start": v(-15.4, 322.12) * mm, "mid": v(-26.63, 320.14) * mm, "end": v(-31.75, 309.96) * mm});
            skArc(sketch, "E267.filletArc", {"start": v(31.75, 298.53) * mm, "mid": v(29.24, 306.1) * mm, "end": v(22.7, 310.7) * mm});
            skSolve(sketch);
        }
        {
            var Q0;
            Q0=qSketchRegion(id+"F28",true);
            extrude(context, id + "F29", {"entities" : qUnion([Q0]), "depth" : 6.35 * mm});
        }
        {
            var Q0;
            {var subQ12=makeQuery(id+"F27.opExtrude","CAP_EDGE",EDGE,{"disambiguationData":[OSD([sQuery(id+"F26.wireOp",EDGE,"E241.filletArc")])],"isStart":false});Q0=makeQuery(id+"F28.imprint","IMPRINT",FACE,{"disambiguationData":[TD([[makeQuery(id+"F28.imprint","IMPRINT",EDGE,{"derivedFrom":subQ12}),1.0]])]});}
            var sketch = newSketch(context, id + "F30", { "sketchPlane" : qUnion([Q0])});
            skPoint(sketch, "E268", {"position": v(0, 0) * mm});
            skPoint(sketch, "E269", {"position": v(-34.93, 0) * mm});
            skPoint(sketch, "E270", {"position": v(-34.93, -280.99) * mm});
            skPoint(sketch, "E271", {"position": v(34.93, 0) * mm});
            skPoint(sketch, "E272", {"position": v(34.93, -303.21) * mm});
            skLineSegment(sketch, "E273", {"start": v(-34.93, 0) * mm, "end": v(-34.93, -271.7) * mm});
            skLineSegment(sketch, "E274", {"start": v(-26.08, -283.8) * mm, "end": v(18.37, -297.95) * mm});
            skLineSegment(sketch, "E275", {"start": v(34.93, -285.84) * mm, "end": v(34.93, 0) * mm});
            skArc(sketch, "E276.filletArc", {"start": v(-34.93, -271.7) * mm, "mid": v(-32.48, -279.2) * mm, "end": v(-26.08, -283.8) * mm});
            skArc(sketch, "E277.filletArc", {"start": v(18.37, -297.95) * mm, "mid": v(29.72, -296.1) * mm, "end": v(34.92, -285.84) * mm});
            skPoint(sketch, "E278.MirrorP", {"position": v(-2087.8, 736.08) * mm});
            skPoint(sketch, "E279", {"position": v(-34.93, 328.61) * mm});
            skPoint(sketch, "E280", {"position": v(34.92, 306.39) * mm});
            skLineSegment(sketch, "E281", {"start": v(-34.93, 0) * mm, "end": v(-34.93, 311.24) * mm});
            skLineSegment(sketch, "E282", {"start": v(-18.37, 323.35) * mm, "end": v(26.08, 309.2) * mm});
            skLineSegment(sketch, "E283", {"start": v(34.92, 297.1) * mm, "end": v(34.93, 0) * mm});
            skArc(sketch, "E284.filletArc", {"start": v(-18.37, 323.35) * mm, "mid": v(-29.72, 321.5) * mm, "end": v(-34.93, 311.24) * mm});
            skArc(sketch, "E285.filletArc", {"start": v(34.92, 297.1) * mm, "mid": v(32.48, 304.6) * mm, "end": v(26.08, 309.2) * mm});
            skSolve(sketch);
        }
        {
            var Q0;
            Q0=qSketchRegion(id+"F30",true);
            extrude(context, id + "F31", {"entities" : qUnion([Q0]), "depth" : 6.35 * mm});
        }
        {
            var Q0;
            Q0=makeQuery(id+"F31.opExtrude","CAP_FACE",FACE,{"disambiguationData":[OSD([sQuery(id+"F30.wireOp",EDGE,"E273"),sQuery(id+"F30.wireOp",EDGE,"E274"),sQuery(id+"F30.wireOp",EDGE,"E275"),sQuery(id+"F30.wireOp",EDGE,"E276.filletArc"),sQuery(id+"F30.wireOp",EDGE,"E277.filletArc"),sQuery(id+"F30.wireOp",EDGE,"E281"),sQuery(id+"F30.wireOp",EDGE,"E282"),sQuery(id+"F30.wireOp",EDGE,"E283"),sQuery(id+"F30.wireOp",EDGE,"E284.filletArc"),sQuery(id+"F30.wireOp",EDGE,"E285.filletArc")])],"isStart":false});
            var sketch = newSketch(context, id + "F32", { "sketchPlane" : qUnion([Q0])});
            skPoint(sketch, "E286", {"position": v(0, 0) * mm});
            skPoint(sketch, "E287", {"position": v(-38.1, 0) * mm});
            skPoint(sketch, "E288", {"position": v(-38.1, -279.4) * mm});
            skPoint(sketch, "E289", {"position": v(38.1, 0) * mm});
            skPoint(sketch, "E290", {"position": v(38.1, -304.8) * mm});
            skLineSegment(sketch, "E291", {"start": v(-38.1, 0) * mm, "end": v(-38.1, -270.25) * mm});
            skLineSegment(sketch, "E292", {"start": v(-29.42, -282.3) * mm, "end": v(21.38, -299.23) * mm});
            skLineSegment(sketch, "E293", {"start": v(38.1, -287.18) * mm, "end": v(38.1, 0) * mm});
            skArc(sketch, "E294.filletArc", {"start": v(-38.1, -270.25) * mm, "mid": v(-35.7, -277.67) * mm, "end": v(-29.42, -282.3) * mm});
            skArc(sketch, "E295.filletArc", {"start": v(21.38, -299.23) * mm, "mid": v(32.83, -297.48) * mm, "end": v(38.1, -287.18) * mm});
            skPoint(sketch, "E296.MirrorP", {"position": v(-2058.68, 783.5) * mm});
            skPoint(sketch, "E297", {"position": v(-38.1, 330.2) * mm});
            skPoint(sketch, "E298", {"position": v(38.1, 304.8) * mm});
            skLineSegment(sketch, "E299", {"start": v(-38.1, 0) * mm, "end": v(-38.1, 312.58) * mm});
            skLineSegment(sketch, "E300", {"start": v(-21.38, 324.63) * mm, "end": v(29.42, 307.7) * mm});
            skLineSegment(sketch, "E301", {"start": v(38.1, 295.65) * mm, "end": v(38.1, 0) * mm});
            skArc(sketch, "E302.filletArc", {"start": v(-21.38, 324.63) * mm, "mid": v(-32.83, 322.88) * mm, "end": v(-38.1, 312.58) * mm});
            skArc(sketch, "E303.filletArc", {"start": v(38.1, 295.65) * mm, "mid": v(35.7, 303.07) * mm, "end": v(29.42, 307.7) * mm});
            skSolve(sketch);
        }
        {
            var Q0;
            Q0=qSketchRegion(id+"F32",true);
            extrude(context, id + "F33", {"entities" : qUnion([Q0]), "depth" : 6.35 * mm});
        }
        {
            var Q0;
            Q0=qCreatedBy(makeId("Top.planeOp"),FACE);
            var sketch = newSketch(context, id + "F34", { "sketchPlane" : qUnion([Q0])});
            skLineSegment(sketch, "E304", {"start": v(0, 0) * mm, "end": v(0, -271) * mm, "construction": true});
            skCircle(sketch, "E305", {"center": v(0, -257.95) * mm, "radius": 8.8 * mm});
            skCircle(sketch, "E306.0.1.0", {"center": v(0, -196.99) * mm, "radius": 8.8 * mm});
            skCircle(sketch, "E306.0.2.0", {"center": v(0, -136.03) * mm, "radius": 8.8 * mm});
            skCircle(sketch, "E306.0.3.0", {"center": v(0, -75.07) * mm, "radius": 8.8 * mm});
            skCircle(sketch, "E306.0.4.0", {"center": v(0, -14.1) * mm, "radius": 8.8 * mm});
            skLineSegment(sketch, "E306.direction1", {"start": v(0, -257.95) * mm, "end": v(25.4, -257.95) * mm, "construction": true});
            skLineSegment(sketch, "E306.direction2", {"start": v(0, -257.95) * mm, "end": v(0, -196.99) * mm, "construction": true});
            skLineSegment(sketch, "E307.MirrorCS", {"start": v(0, 257.95) * mm, "end": v(0, 196.99) * mm, "construction": true});
            skLineSegment(sketch, "E308.MirrorCS", {"start": v(0, 0) * mm, "end": v(0, 271) * mm, "construction": true});
            skLineSegment(sketch, "E309.MirrorCS", {"start": v(0, 257.95) * mm, "end": v(25.4, 257.95) * mm, "construction": true});
            skCircle(sketch, "E310.MirrorC", {"center": v(0, 14.1) * mm, "radius": 8.8 * mm});
            skCircle(sketch, "E311.MirrorC", {"center": v(0, 136.03) * mm, "radius": 8.8 * mm});
            skCircle(sketch, "E312.MirrorC", {"center": v(0, 75.07) * mm, "radius": 8.8 * mm});
            skCircle(sketch, "E313.MirrorC", {"center": v(0, 257.95) * mm, "radius": 8.8 * mm});
            skCircle(sketch, "E314.MirrorC", {"center": v(0, 196.99) * mm, "radius": 8.8 * mm});
            skSolve(sketch);
        }
        {
            var Q0;
            Q0=qSketchRegion(id+"F34",true);
            extrude(context, id + "F35", {"entities" : qUnion([Q0]), "operationType" : NewBodyOperationType.ADD, "endBound" : BoundingType.SYMMETRIC, "depth" : 25.4 * mm, "hasDraft" : true, "draftAngle" : 20 * degree});
        }
    });
